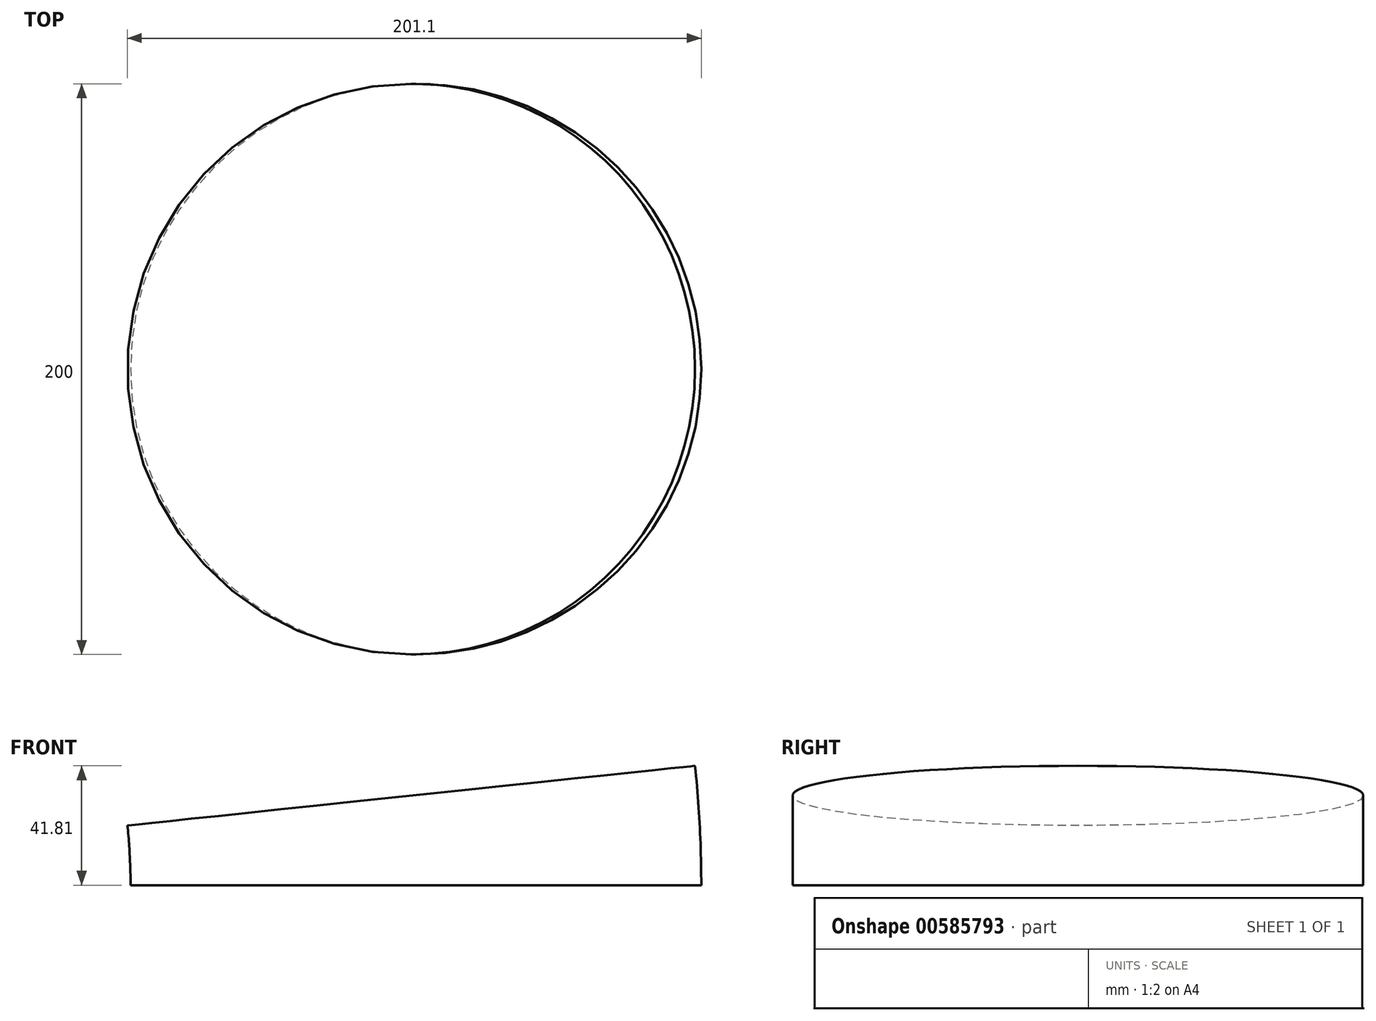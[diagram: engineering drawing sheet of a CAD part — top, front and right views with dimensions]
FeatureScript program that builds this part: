
annotation { "Feature Type Name" : "Feature", "Feature Type Description" : "" }
export const myFeature = defineFeature(function(context is Context, id is Id, definition is map)
    precondition{}
    {
        {
            var Q0;
            Q0=qCreatedBy(makeId("Top.planeOp"),FACE);
            var sketch = newSketch(context, id + "F0", { "sketchPlane" : qUnion([Q0])});
            skLineSegment(sketch, "E0", {"start": v(0, 0) * mm, "end": v(0, -85.93) * mm});
            skCircle(sketch, "E1", {"center": v(300, 0) * mm, "radius": 100 * mm});
            skLineSegment(sketch, "E2", {"start": v(0, 0) * mm, "end": v(300, 0) * mm});
            skSolve(sketch);
        }
        {
            var Q0;
            Q0=makeQuery(id+"F0.imprint","IMPRINT",FACE,{"disambiguationData":[TD([[makeQuery(id+"F0.imprint","IMPRINT",EDGE,{"derivedFrom":sQuery(id+"F0.wireOp",EDGE,"E1")}),1.0]])]});
            var Q1;
            Q1=sQuery(id+"F0.wireOp",EDGE,"E0");
            revolve(context, id + "F1", {"surfaceOperationType" : NewSurfaceOperationType.NEW, "entities" : qUnion([Q0]), "axis" : qUnion([Q1]), "revolveType" : RevolveType.ONE_DIRECTION, "angle" : 6 * degree});
        }
    });
